# Revit family: 2210L-V2
name_source: partatom
category: Generic Models
revit_build: Autodesk Revit 2015 (Build: 20140606_1530(x64)
units: mm (PartAtom-declared; Revit-internal decimal feet)

## types (1)
- 2210L-V2
    Category = Sink mixer
    Default Elevation = 1219 mm
    Description = French manufacturer Delabie is a leader in the European sanitary ware market for non-domestic places. Water controls, solutions for disabled people, sanitary ware, for schools, leisure centres, offices, hospitals, airports…
    Diameter = 15 mm  [stored 0.0492126 ft]
    Features = Deck-mounted mechanical sink mixer without pop-up waste.  Swivelling spout H. 145mm L. 220mm with hygienic flow straightener.  Ø 40mm ceramic cartridge.  Pre-set maximum temperature limiter.  Body and spout with smooth interiors. Flow rate limited to 9 lpm at 3 bar.  Hygiene control lever L. 200mm.  Reinforced fixing via 2 stainless steel rods. PEX F3/8".
    Finish = Chrome-plated
    FlowRate = 9 lpm
    Grade = ACS, PZH
    IntegralAccessories = PEX flexibles
    IntegralAccessoryOptions = Wastes
    Manufacturer = DELABIE
    ManufacturerName = DELABIE
    Material = Brass
    Model = Mechanical sink mixer H.145mm L.220mm
    Model number = 2510
    Name = 2210L
    NominalHeight = 14,5 cm
    NominalWidth = 22 cm
    Operation = Mechanical mixer
    Polantis code = DLB090019
    ProductInformation = http://www.delabie.com
    SerialNumber = 3456330116602
    URL = http://www.delabie.com
    WarrantyDescription = Any manufacturing defect
    WarrantyDurationUnit = 10 years
    WaterSupplyTemperatureMaximum = 55°C-85° (∆50°C : CW/HW)

note: [stored X ft] marks values corroborated as IEEE doubles in the binary element streams (Revit-internal decimal feet)

## geometry (parser evidence)
native form markers: Sweep x3
no freeform markers — native parametric forms only
